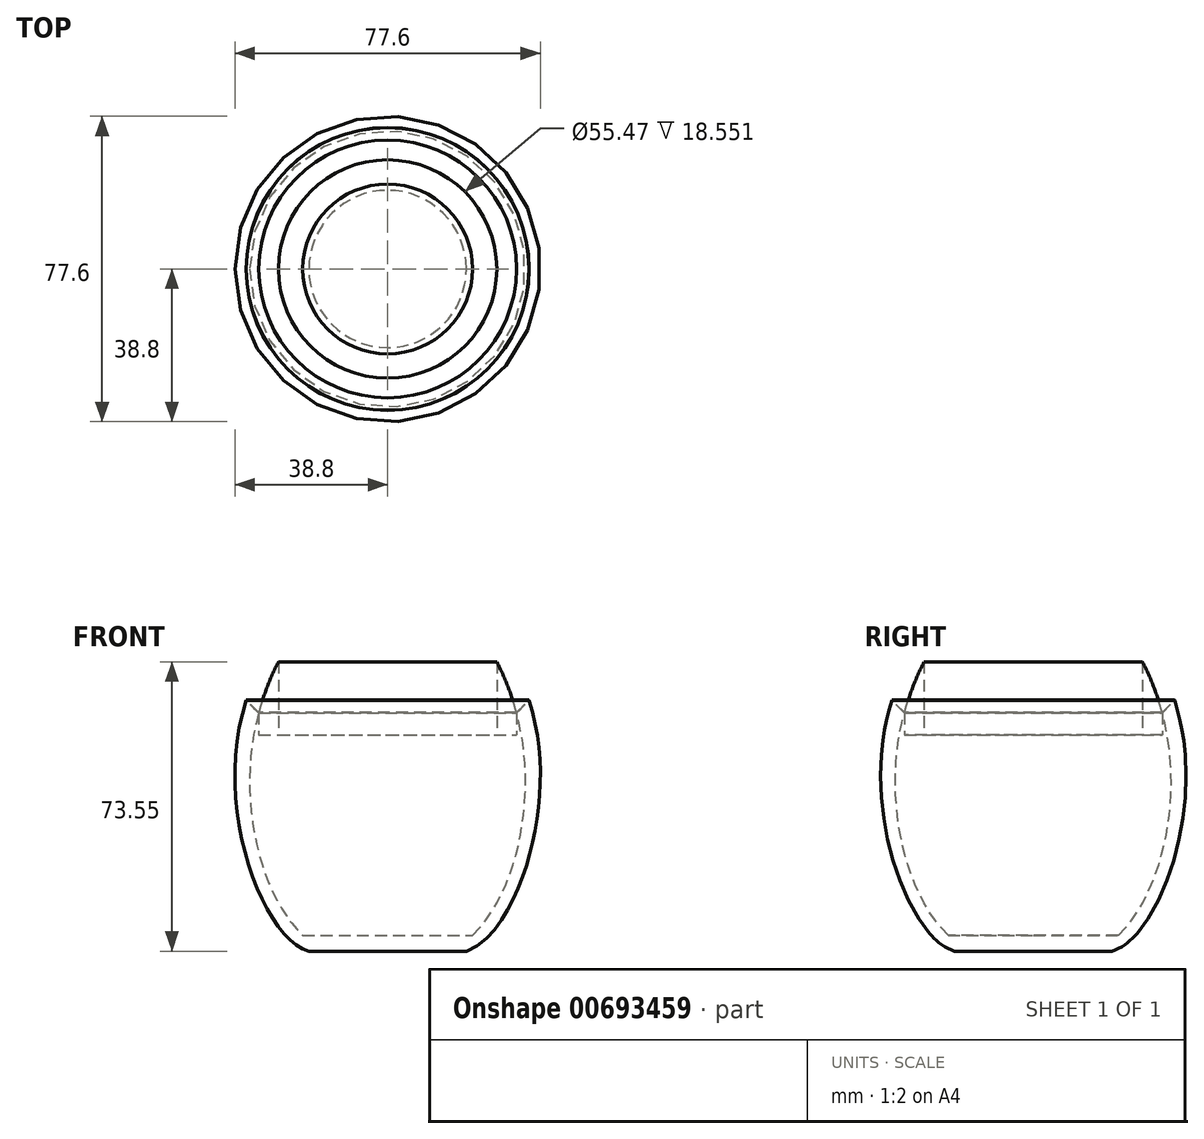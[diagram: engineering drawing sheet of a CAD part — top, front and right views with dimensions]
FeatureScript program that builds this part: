
annotation { "Feature Type Name" : "Feature", "Feature Type Description" : "" }
export const myFeature = defineFeature(function(context is Context, id is Id, definition is map)
    precondition{}
    {
        {
            var Q0;
            Q0=qCreatedBy(makeId("Front.planeOp"),FACE);
            var sketch = newSketch(context, id + "F0", { "sketchPlane" : qUnion([Q0])});
            skLineSegment(sketch, "E0", {"start": v(-16, 0) * mm, "end": v(-20, 0) * mm});
            skLineSegment(sketch, "E1", {"start": v(0, 0) * mm, "end": v(0, 100) * mm, "construction": true});
            skFitSpline(sketch, "E2", {"points": [v(0, 100) * mm, v(-38, 55) * mm, v(-20, 0) * mm], "startDerivative": vector(-89.6, 0) * mm, "endDerivative": vector(65.84, -19.41) * mm});
            skFitSpline(sketch, "E3", {"points": [v(0, 96) * mm, v(-34, 55) * mm, v(-16, 0) * mm], "startDerivative": vector(-91.9, 0) * mm, "endDerivative": vector(81.54, -40.01) * mm});
            skLineSegment(sketch, "E4", {"start": v(0, 100) * mm, "end": v(0, 96) * mm});
            skLineSegment(sketch, "E5", {"start": v(-16, 0) * mm, "end": v(0, 0) * mm});
            skLineSegment(sketch, "E6", {"start": v(0, 4) * mm, "end": v(-21.58, 4) * mm});
            skLineSegment(sketch, "E7", {"start": v(-35.93, 63.68) * mm, "end": v(-32.76, 60.52) * mm});
            skLineSegment(sketch, "E8", {"start": v(-35.9, 63.8) * mm, "end": v(-32.73, 60.63) * mm});
            skLineSegment(sketch, "E9", {"start": v(-32.73, 60.63) * mm, "end": v(-32.73, 55) * mm});
            skLineSegment(sketch, "E10", {"start": v(-32.73, 55) * mm, "end": v(-27.73, 55) * mm});
            skLineSegment(sketch, "E11", {"start": v(-27.73, 55) * mm, "end": v(-27.73, 73.55) * mm});
            skFitSpline(sketch, "E12.trimOffspring", {"points": [v(0, 100) * mm, v(-38, 55) * mm, v(-20, 0) * mm], "startDerivative": vector(-89.6, 0) * mm, "endDerivative": vector(65.84, -19.41) * mm});
            skLineSegment(sketch, "E13", {"start": v(0, 4) * mm, "end": v(0, 0) * mm});
            skSolve(sketch);
        }
        {
            var Q0;
            {var subQ3=sQuery(id+"F0.wireOp",EDGE,"E0");Q0=makeQuery(id+"F0.imprint","IMPRINT",FACE,{"disambiguationData":[TD([[makeQuery(id+"F0.imprint","IMPRINT",EDGE,{"derivedFrom":subQ3}),-1.0]])]});}
            var Q1;
            {var subQ0=sQuery(id+"F0.wireOp",EDGE,"E5");Q1=makeQuery(id+"F0.imprint","IMPRINT",FACE,{"disambiguationData":[TD([[makeQuery(id+"F0.imprint","IMPRINT",EDGE,{"derivedFrom":subQ0}),1.0]])]});}
            var Q2;
            Q2=sQuery(id+"F0.wireOp",EDGE,"E1");
            revolve(context, id + "F1", {"entities" : qUnion([Q0, Q1]), "axis" : qUnion([Q2]), "revolveType" : RevolveType.FULL});
        }
        {
            var Q0;
            Q0=makeQuery(id+"F0.imprint","IMPRINT",FACE,{"disambiguationData":[TD([[makeQuery(id+"F0.imprint","IMPRINT",EDGE,{"derivedFrom":sQuery(id+"F0.wireOp",EDGE,"E2")}),1.0]])]});
            var Q1;
            {var subQ0=sQuery(id+"F0.wireOp",EDGE,"E9");Q1=makeQuery(id+"F0.imprint","IMPRINT",FACE,{"disambiguationData":[TD([[makeQuery(id+"F0.imprint","IMPRINT",EDGE,{"derivedFrom":subQ0}),1.0]])]});}
            var Q2;
            Q2=sQuery(id+"F0.wireOp",EDGE,"E1");
            revolve(context, id + "F2", {"entities" : qUnion([Q0, Q1]), "axis" : qUnion([Q2]), "revolveType" : RevolveType.FULL});
        }
    });
